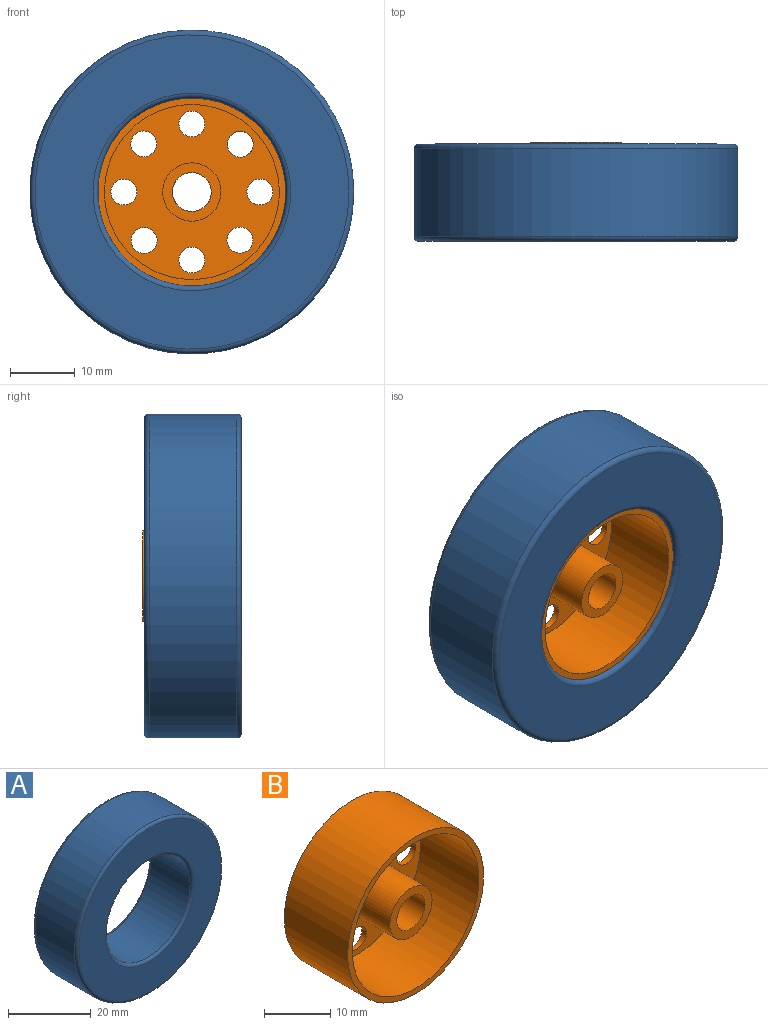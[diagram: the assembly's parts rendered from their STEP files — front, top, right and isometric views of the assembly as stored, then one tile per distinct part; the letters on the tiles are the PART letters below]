
ASSEMBLY  parts=2 mates=1
PART A: 8 faces, bbox 54.1x15x54.1 mm
  f0: torus R=24.25mm, axis (0,-1,0), area 183mm2, adj f1,f7
  f1: plane 48.5x48.5mm, normal (0,1,0), area 1116.8mm2, adj f0,f2
  f2: torus R=15.25mm, axis (0,-1,0), area 109.3mm2, adj f1,f3
  f3: cylinder r=14.5mm len=29mm, axis (0,-1,0), area 1229.9mm2, adj f2,f4
  f4: torus R=15.25mm, axis (0,-1,0), area 109.3mm2, adj f3,f5
  f5: plane 48.5x48.5mm, normal (0,-1,0), area 1116.8mm2, adj f4,f6
  f6: torus R=24.25mm, axis (0,-1,0), area 183mm2, adj f5,f7
  f7: cylinder r=25mm len=50mm, axis (0,-1,0), area 2120.6mm2, adj f0,f6
PART B: 20 faces, bbox 29x14.5x29 mm
  f0: plane 29x29mm, normal (0,1,0), area 406.1mm2, adj f1,f3,f9,f10,f11,f12,f13,f14
  f1: cylinder r=14.5mm len=29mm, axis (0,-1,0), area 1229.9mm2, adj f0,f2
  f2: plane 29x29mm, normal (0,-1,0), area 88mm2, adj f1,f6
  f3: cylinder r=7mm len=14mm, axis (0,-1,0), area 44mm2, adj f0,f4
  f4: plane 14x14mm, normal (0,1,0), area 103.7mm2, adj f3,f19
  f5: plane 27x27mm, normal (0,-1,0), area 408.4mm2, adj f6,f7,f9,f10,f11,f12,f13,f14
  f6: cylinder r=13.5mm len=27mm, axis (0,-1,0), area 1060.3mm2, adj f2,f5
  f7: cylinder r=4.5mm len=11.5mm, axis (0,-1,0), area 325.2mm2, adj f5,f8
  f8: plane 9x9mm, normal (0,-1,0), area 35.3mm2, adj f7,f17
  f9: cylinder r=2mm len=4mm, axis (0,1,0), area 12.6mm2, adj f0,f5
  f10: cylinder r=2mm len=4mm, axis (0,1,0), area 12.6mm2, adj f0,f5
  f11: cylinder r=2mm len=4mm, axis (0,1,0), area 12.6mm2, adj f0,f5
  f12: cylinder r=2mm len=4mm, axis (0,1,0), area 12.6mm2, adj f0,f5
  f13: cylinder r=2mm len=4mm, axis (0,1,0), area 12.6mm2, adj f0,f5
  f14: cylinder r=2mm len=4mm, axis (0,1,0), area 12.6mm2, adj f0,f5
  f15: cylinder r=2mm len=4mm, axis (0,1,0), area 12.6mm2, adj f0,f5
  f16: cylinder r=2mm len=4mm, axis (0,-1,0), area 12.6mm2, adj f0,f5
  f17: cylinder r=3mm len=12.5mm, axis (0,1,0), area 235.6mm2, adj f8,f18
  f18: plane 8x8mm, normal (0,1,0), area 22mm2, adj f17,f19
  f19: cylinder r=4mm len=8mm, axis (0,1,0), area 25.1mm2, adj f4,f18
PLACE A at identity fixed
PLACE B t=(0,-8.25,0)mm
MATE fastened B.f1 <-> A.f0  axis (0,-1,0) through (0,-14.25,0)mm
